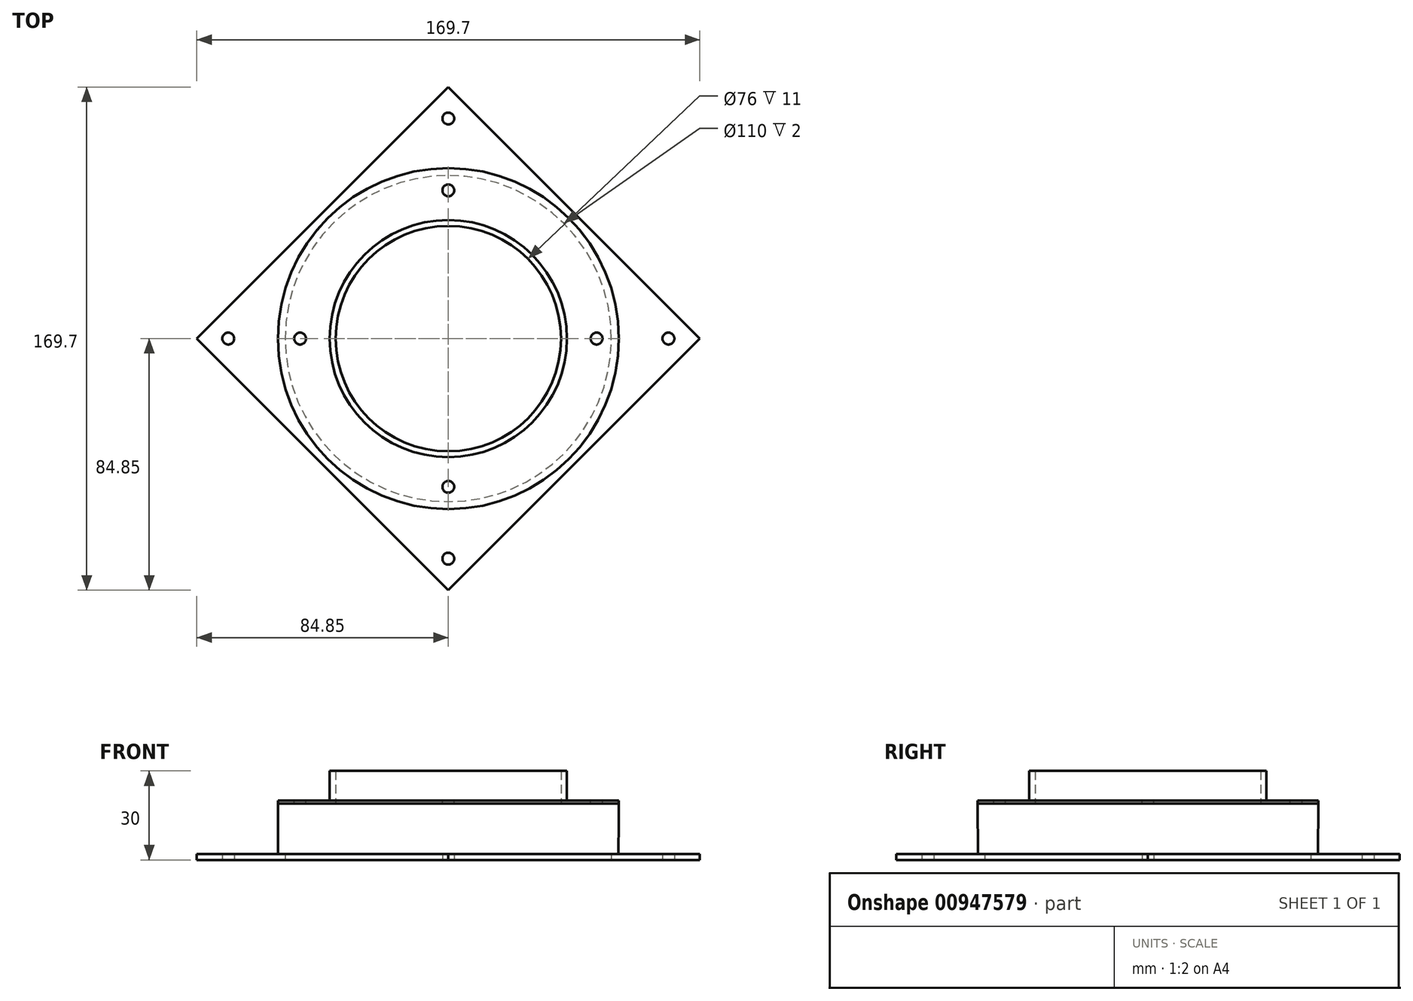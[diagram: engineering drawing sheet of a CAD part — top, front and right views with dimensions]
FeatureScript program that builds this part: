
annotation { "Feature Type Name" : "Feature", "Feature Type Description" : "" }
export const myFeature = defineFeature(function(context is Context, id is Id, definition is map)
    precondition{}
    {
        {
            var Q0;
            Q0=qCreatedBy(makeId("Top.planeOp"),FACE);
            var sketch = newSketch(context, id + "F0", { "sketchPlane" : qUnion([Q0])});
            skCircle(sketch, "E0", {"center": v(0, 0) * mm, "radius": 40 * mm});
            skCircle(sketch, "E1", {"center": v(0, 0) * mm, "radius": 38 * mm});
            skSolve(sketch);
        }
        {
            var Q0;
            Q0 = qSketchRegion(id + "F0", true);
            extrude(context, id + "F1", {"entities" : qUnion([Q0]), "depth" : 10 * mm, "offsetDistance" : 25 * mm});
        }
        {
            var Q0;
            Q0=makeQuery(id+"F1.opExtrude","CAP_FACE",FACE,{"disambiguationData":[OSD([sQuery(id+"F0.wireOp",EDGE,"E0"),sQuery(id+"F0.wireOp",EDGE,"E1")])],"isStart":true});
            var sketch = newSketch(context, id + "F2", { "sketchPlane" : qUnion([Q0])});
            skCircle(sketch, "E2", {"center": v(0, 0) * mm, "radius": 38 * mm});
            skCircle(sketch, "E3", {"center": v(0, 0) * mm, "radius": 57.5 * mm});
            skCircle(sketch, "E4", {"center": v(0, 50) * mm, "radius": 2 * mm});
            skCircle(sketch, "E5.1.0", {"center": v(-50, 0) * mm, "radius": 2 * mm});
            skCircle(sketch, "E5.2.0", {"center": v(0, -50) * mm, "radius": 2 * mm});
            skCircle(sketch, "E5.3.0", {"center": v(50, 0) * mm, "radius": 2 * mm});
            skSolve(sketch);
        }
        {
            var Q0;
            Q0 = qSketchRegion(id + "F2", true);
            extrude(context, id + "F3", {"entities" : qUnion([Q0]), "operationType" : NewBodyOperationType.ADD, "depth" : 1 * mm, "offsetDistance" : 25 * mm});
        }
        {
            var Q0;
            Q0=qCreatedBy(makeId("Top.planeOp"),FACE);
            cPlane(context, id + "F4", {"entities" : qUnion([Q0]), "cplaneType" : CPlaneType.OFFSET, "offset" : 20 * mm, "oppositeDirection" : true, "width" : 150 * mm, "height" : 150 * mm});
        }
        {
            var Q0;
            Q0=qCreatedBy(id+"F4.planeOp",FACE);
            var sketch = newSketch(context, id + "F5", { "sketchPlane" : qUnion([Q0])});
            skCircle(sketch, "E6", {"center": v(0, 0) * mm, "radius": 55 * mm});
            skCircle(sketch, "E7", {"center": v(0, -74.23) * mm, "radius": 2 * mm});
            skCircle(sketch, "E8.1.0", {"center": v(74.23, 0) * mm, "radius": 2 * mm});
            skCircle(sketch, "E8.2.0", {"center": v(0, 74.23) * mm, "radius": 2 * mm});
            skCircle(sketch, "E8.3.0", {"center": v(-74.23, 0) * mm, "radius": 2 * mm});
            skLineSegment(sketch, "E9", {"start": v(-84.85, 0) * mm, "end": v(0, 84.85) * mm});
            skLineSegment(sketch, "E10", {"start": v(0, 84.85) * mm, "end": v(84.85, 0) * mm});
            skLineSegment(sketch, "E11", {"start": v(84.85, 0) * mm, "end": v(0, -84.85) * mm});
            skLineSegment(sketch, "E12", {"start": v(0, -84.85) * mm, "end": v(-84.85, 0) * mm});
            skLineSegment(sketch, "E13", {"start": v(-84.85, 0) * mm, "end": v(84.85, 0) * mm, "construction": true});
            skSolve(sketch);
        }
        {
            var Q0;
            Q0 = qSketchRegion(id + "F5", true);
            extrude(context, id + "F6", {"entities" : qUnion([Q0]), "depth" : 2 * mm, "offsetDistance" : 25 * mm});
        }
        {
            var Q0;
            Q0=makeQuery(id+"F6.opExtrude","CAP_FACE",FACE,{"disambiguationData":[OSD([sQuery(id+"F5.wireOp",EDGE,"E6"),sQuery(id+"F5.wireOp",EDGE,"E7"),sQuery(id+"F5.wireOp",EDGE,"E8.1.0"),sQuery(id+"F5.wireOp",EDGE,"E8.2.0"),sQuery(id+"F5.wireOp",EDGE,"E8.3.0"),sQuery(id+"F5.wireOp",EDGE,"E9"),sQuery(id+"F5.wireOp",EDGE,"E10"),sQuery(id+"F5.wireOp",EDGE,"E11"),sQuery(id+"F5.wireOp",EDGE,"E12")])],"isStart":false});
            var sketch = newSketch(context, id + "F7", { "sketchPlane" : qUnion([Q0])});
            skCircle(sketch, "E14", {"center": v(0, 0) * mm, "radius": 57.39 * mm});
            skSolve(sketch);
        }
        {
            var Q0;
            Q0=makeQuery(id+"F3.opExtrude","CAP_FACE",FACE,{"disambiguationData":[OSD([sQuery(id+"F2.wireOp",EDGE,"E2"),sQuery(id+"F2.wireOp",EDGE,"E3"),sQuery(id+"F2.wireOp",EDGE,"E4"),sQuery(id+"F2.wireOp",EDGE,"E5.1.0"),sQuery(id+"F2.wireOp",EDGE,"E5.2.0"),sQuery(id+"F2.wireOp",EDGE,"E5.3.0")])],"isStart":false});
            var sketch = newSketch(context, id + "F8", { "sketchPlane" : qUnion([Q0])});
            skCircle(sketch, "E15", {"center": v(0, 0) * mm, "radius": 57.5 * mm});
            skSolve(sketch);
        }
        {
            var Q0;
            Q0 = qSketchRegion(id + "F7", true);
            var Q1;
            Q1 = qSketchRegion(id + "F8", true);
            loft(context, id + "F9", {"sheetProfilesArray" : [{ "sheetProfileEntities" : qUnion([Q0]) }, { "sheetProfileEntities" : qUnion([Q1]) }]});
        }
    });
